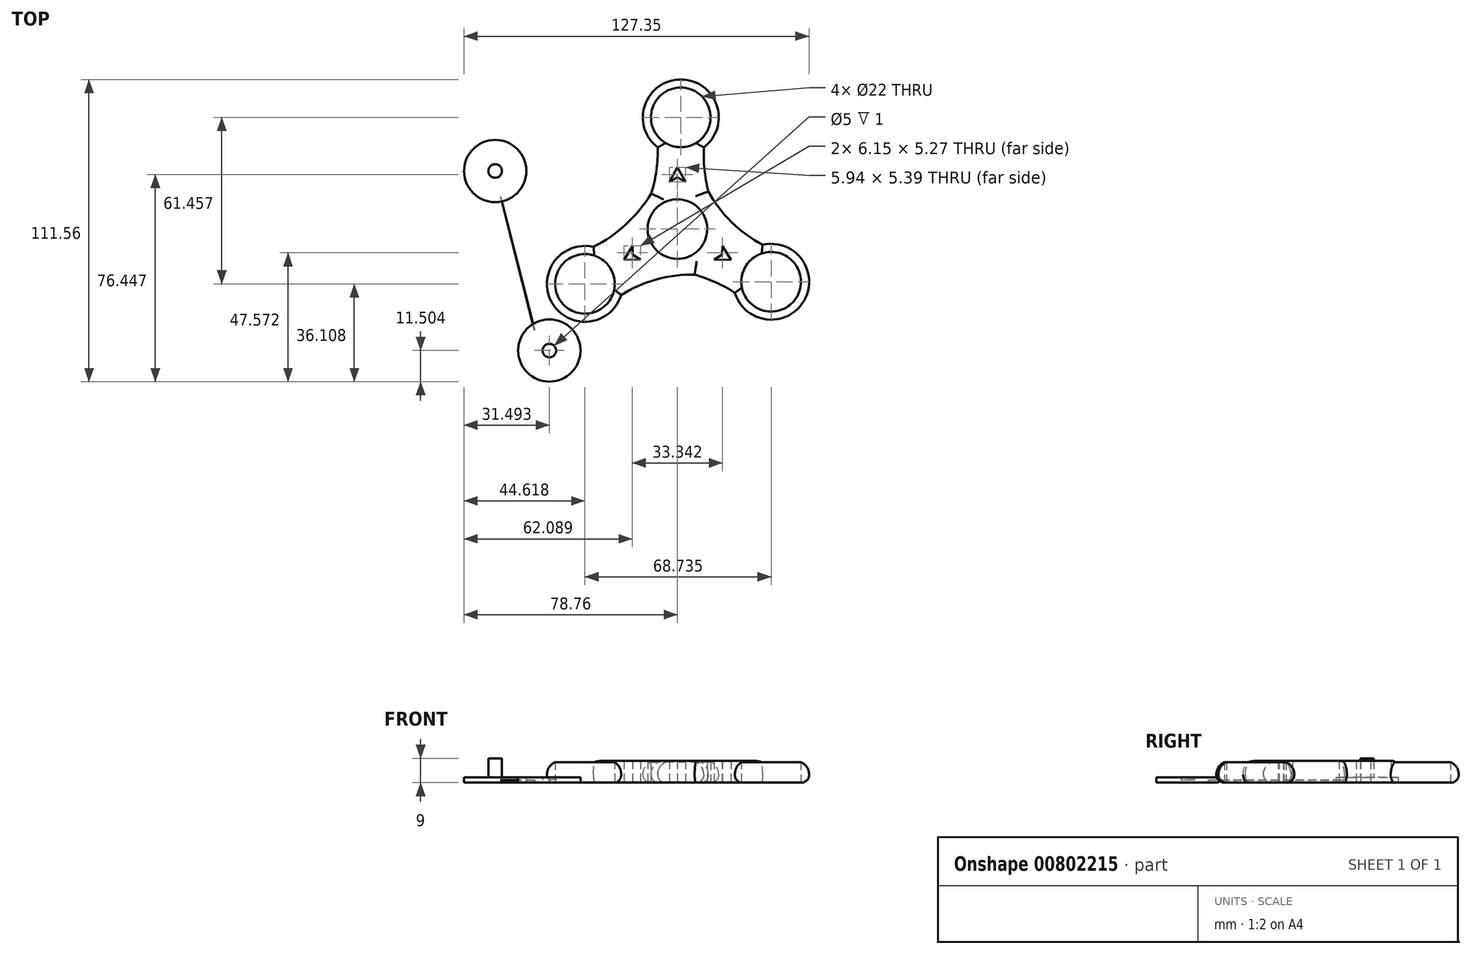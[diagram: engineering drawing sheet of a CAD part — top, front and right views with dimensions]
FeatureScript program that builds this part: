
annotation { "Feature Type Name" : "Feature", "Feature Type Description" : "" }
export const myFeature = defineFeature(function(context is Context, id is Id, definition is map)
    precondition{}
    {
        {
            var Q0;
            Q0=qCreatedBy(makeId("Top.planeOp"),FACE);
            var sketch = newSketch(context, id + "F0", { "sketchPlane" : qUnion([Q0])});
            skCircle(sketch, "E0", {"center": v(0, 0) * mm, "radius": 0.92 * mm});
            skCircle(sketch, "E1", {"center": v(0, 0) * mm, "radius": 11 * mm});
            skArc(sketch, "E2", {"start": v(-16.3, 0) * mm, "mid": v(-9.31, 14.32) * mm, "end": v(-7.3, 30.13) * mm});
            skArc(sketch, "E3", {"start": v(9.79, 30.13) * mm, "mid": v(1.24, 55.22) * mm, "end": v(-7.3, 30.13) * mm});
            skArc(sketch, "E4", {"start": v(9.79, 30.13) * mm, "mid": v(11.27, 14.51) * mm, "end": v(17.24, 0) * mm});
            skArc(sketch, "E5.1.0", {"start": v(-30.99, -6.6) * mm, "mid": v(-46.27, -27.23) * mm, "end": v(-20.75, -24.32) * mm});
            skArc(sketch, "E5.1.1", {"start": v(-30.99, -6.6) * mm, "mid": v(-18.2, 2.5) * mm, "end": v(-8.62, 14.93) * mm});
            skArc(sketch, "E5.1.2", {"start": v(9.85, -17.06) * mm, "mid": v(-6.05, -18.16) * mm, "end": v(-20.75, -24.32) * mm});
            skArc(sketch, "E5.2.0", {"start": v(21.2, -23.54) * mm, "mid": v(46.72, -26.45) * mm, "end": v(31.44, -5.81) * mm});
            skArc(sketch, "E5.2.1", {"start": v(21.2, -23.54) * mm, "mid": v(6.93, -17.01) * mm, "end": v(-8.62, -14.93) * mm});
            skArc(sketch, "E5.2.2", {"start": v(9.85, 17.06) * mm, "mid": v(18.75, 3.84) * mm, "end": v(31.44, -5.81) * mm});
            skCircle(sketch, "E6", {"center": v(1.24, 41.22) * mm, "radius": 11 * mm});
            skCircle(sketch, "E7", {"center": v(-34.14, -20.23) * mm, "radius": 11 * mm});
            skCircle(sketch, "E8", {"center": v(34.6, -19.45) * mm, "radius": 11 * mm});
            skLineSegment(sketch, "E9", {"start": v(0, 22.8) * mm, "end": v(-2.97, 17.41) * mm});
            skLineSegment(sketch, "E10", {"start": v(0, 22.8) * mm, "end": v(2.97, 17.41) * mm});
            skLineSegment(sketch, "E11", {"start": v(2.97, 17.41) * mm, "end": v(0, 19.05) * mm});
            skLineSegment(sketch, "E12", {"start": v(0, 19.05) * mm, "end": v(-2.97, 17.41) * mm});
            skLineSegment(sketch, "E13.1.0", {"start": v(-19.75, -11.4) * mm, "end": v(-16.56, -6.13) * mm});
            skLineSegment(sketch, "E13.1.1", {"start": v(-19.75, -11.4) * mm, "end": v(-13.6, -11.28) * mm});
            skLineSegment(sketch, "E13.1.2", {"start": v(-16.5, -9.52) * mm, "end": v(-13.6, -11.28) * mm});
            skLineSegment(sketch, "E13.1.3", {"start": v(-16.56, -6.13) * mm, "end": v(-16.5, -9.52) * mm});
            skLineSegment(sketch, "E13.2.0", {"start": v(19.75, -11.4) * mm, "end": v(13.6, -11.28) * mm});
            skLineSegment(sketch, "E13.2.1", {"start": v(19.75, -11.4) * mm, "end": v(16.56, -6.13) * mm});
            skLineSegment(sketch, "E13.2.2", {"start": v(16.5, -9.52) * mm, "end": v(16.56, -6.13) * mm});
            skLineSegment(sketch, "E13.2.3", {"start": v(13.6, -11.28) * mm, "end": v(16.5, -9.52) * mm});
            skSolve(sketch);
        }
        {
            var Q0;
            Q0 = qSketchRegion(id + "F0", true);
            extrude(context, id + "F1", {"entities" : qUnion([Q0]), "depth" : 8 * mm, "offsetDistance" : 25 * mm});
        }
        {
            var Q0;
            Q0=makeQuery(id+"F1.opExtrude","CAP_EDGE",EDGE,{"disambiguationData":[OSD([sQuery(id+"F0.wireOp",EDGE,"E3")])],"isStart":false});
            var Q1;
            Q1=makeQuery(id+"F1.opExtrude","CAP_EDGE",EDGE,{"disambiguationData":[OSD([sQuery(id+"F0.wireOp",EDGE,"E4")])],"isStart":false});
            var Q2;
            Q2=makeQuery(id+"F1.opExtrude","CAP_EDGE",EDGE,{"disambiguationData":[OSD([sQuery(id+"F0.wireOp",EDGE,"E5.2.2")])],"isStart":false});
            var Q3;
            Q3=makeQuery(id+"F1.opExtrude","CAP_EDGE",EDGE,{"disambiguationData":[OSD([sQuery(id+"F0.wireOp",EDGE,"E5.2.0")])],"isStart":false});
            var Q4;
            Q4=makeQuery(id+"F1.opExtrude","CAP_EDGE",EDGE,{"disambiguationData":[OSD([sQuery(id+"F0.wireOp",EDGE,"E5.2.1")])],"isStart":false});
            var Q5;
            Q5=makeQuery(id+"F1.opExtrude","CAP_EDGE",EDGE,{"disambiguationData":[OSD([sQuery(id+"F0.wireOp",EDGE,"E5.1.2")])],"isStart":false});
            var Q6;
            Q6=makeQuery(id+"F1.opExtrude","CAP_EDGE",EDGE,{"disambiguationData":[OSD([sQuery(id+"F0.wireOp",EDGE,"E5.1.0")])],"isStart":false});
            var Q7;
            Q7=makeQuery(id+"F1.opExtrude","CAP_EDGE",EDGE,{"disambiguationData":[OSD([sQuery(id+"F0.wireOp",EDGE,"E5.1.1")])],"isStart":false});
            var Q8;
            Q8=makeQuery(id+"F1.opExtrude","CAP_EDGE",EDGE,{"disambiguationData":[OSD([sQuery(id+"F0.wireOp",EDGE,"E2")])],"isStart":false});
            fillet(context, id + "F2", {"entities" : qUnion([Q0, Q1, Q2, Q3, Q4, Q5, Q6, Q7, Q8]), "radius" : 5 * mm, "tangentPropagation" : true, "allowEdgeOverflow" : false});
        }
        {
            var Q0;
            Q0=makeQuery(id+"F1.opExtrude","CAP_EDGE",EDGE,{"disambiguationData":[OSD([sQuery(id+"F0.wireOp",EDGE,"E2")])],"isStart":true});
            var Q1;
            Q1=makeQuery(id+"F1.opExtrude","CAP_EDGE",EDGE,{"disambiguationData":[OSD([sQuery(id+"F0.wireOp",EDGE,"E5.1.1")])],"isStart":true});
            var Q2;
            Q2=makeQuery(id+"F1.opExtrude","CAP_EDGE",EDGE,{"disambiguationData":[OSD([sQuery(id+"F0.wireOp",EDGE,"E5.1.2")])],"isStart":true});
            var Q3;
            Q3=makeQuery(id+"F1.opExtrude","CAP_EDGE",EDGE,{"disambiguationData":[OSD([sQuery(id+"F0.wireOp",EDGE,"E5.2.1")])],"isStart":true});
            var Q4;
            Q4=makeQuery(id+"F1.opExtrude","CAP_EDGE",EDGE,{"disambiguationData":[OSD([sQuery(id+"F0.wireOp",EDGE,"E4")])],"isStart":true});
            var Q5;
            Q5=makeQuery(id+"F1.opExtrude","CAP_EDGE",EDGE,{"disambiguationData":[OSD([sQuery(id+"F0.wireOp",EDGE,"E5.1.0")])],"isStart":true});
            var Q6;
            Q6=makeQuery(id+"F1.opExtrude","CAP_EDGE",EDGE,{"disambiguationData":[OSD([sQuery(id+"F0.wireOp",EDGE,"E5.2.0")])],"isStart":true});
            var Q7;
            Q7=makeQuery(id+"F1.opExtrude","CAP_EDGE",EDGE,{"disambiguationData":[OSD([sQuery(id+"F0.wireOp",EDGE,"E3")])],"isStart":true});
            var Q8;
            Q8=makeQuery(id+"F1.opExtrude","CAP_EDGE",EDGE,{"disambiguationData":[OSD([sQuery(id+"F0.wireOp",EDGE,"E5.2.2")])],"isStart":true});
            fillet(context, id + "F3", {"entities" : qUnion([Q0, Q1, Q2, Q3, Q4, Q5, Q6, Q7, Q8]), "radius" : 2.9 * mm, "tangentPropagation" : true, "allowEdgeOverflow" : false});
        }
        {
            var Q0;
            Q0=qCreatedBy(makeId("Top.planeOp"),FACE);
            var sketch = newSketch(context, id + "F4", { "sketchPlane" : qUnion([Q0])});
            skCircle(sketch, "E14", {"center": v(-67.26, 21.43) * mm, "radius": 11.5 * mm});
            skCircle(sketch, "E15", {"center": v(-67.26, 21.43) * mm, "radius": 2.5 * mm});
            skSolve(sketch);
        }
        {
            var Q0;
            Q0=makeQuery(id+"F4.imprint","IMPRINT",FACE,{"disambiguationData":[TD([[makeQuery(id+"F4.imprint","IMPRINT",EDGE,{"derivedFrom":sQuery(id+"F4.wireOp",EDGE,"E14")}),1.0]])]});
            extrude(context, id + "F5", {"entities" : qUnion([Q0]), "depth" : 2 * mm, "offsetDistance" : 25 * mm});
        }
        {
            var Q0;
            Q0=makeQuery(id+"F4.imprint","IMPRINT",FACE,{"disambiguationData":[TD([[makeQuery(id+"F4.imprint","IMPRINT",EDGE,{"derivedFrom":sQuery(id+"F4.wireOp",EDGE,"E15")}),1.0]])]});
            extrude(context, id + "F6", {"entities" : qUnion([Q0]), "operationType" : NewBodyOperationType.ADD, "depth" : 9 * mm, "offsetDistance" : 25 * mm});
        }
        {
            var Q0;
            Q0=qCreatedBy(makeId("Top.planeOp"),FACE);
            var sketch = newSketch(context, id + "F7", { "sketchPlane" : qUnion([Q0])});
            skCircle(sketch, "E16", {"center": v(-47.27, -44.84) * mm, "radius": 11.5 * mm});
            skCircle(sketch, "E17", {"center": v(-47.27, -44.84) * mm, "radius": 2.5 * mm});
            skSolve(sketch);
        }
        {
            var Q0;
            Q0 = qSketchRegion(id + "F7", true);
            extrude(context, id + "F8", {"entities" : qUnion([Q0]), "depth" : 2 * mm, "offsetDistance" : 25 * mm});
        }
        {
            var Q0;
            Q0=makeQuery(id+"F7.imprint","IMPRINT",FACE,{"disambiguationData":[TD([[makeQuery(id+"F7.imprint","IMPRINT",EDGE,{"derivedFrom":sQuery(id+"F7.wireOp",EDGE,"E17")}),1.0]])]});
            extrude(context, id + "F9", {"entities" : qUnion([Q0]), "operationType" : NewBodyOperationType.ADD, "depth" : 1 * mm, "offsetDistance" : 25 * mm});
        }
        {
            var Q0;
            Q0=qCreatedBy(makeId("Top.planeOp"),FACE);
            var sketch = newSketch(context, id + "F10", { "sketchPlane" : qUnion([Q0])});
            skLineSegment(sketch, "E18", {"start": v(-65.26, 12.04) * mm, "end": v(-52.63, -37.25) * mm});
            skLineSegment(sketch, "E19", {"start": v(-52.63, -37.25) * mm, "end": v(-52.85, -37.3) * mm});
            skLineSegment(sketch, "E20", {"start": v(-52.85, -37.3) * mm, "end": v(-65.26, 12.04) * mm});
            skSolve(sketch);
        }
        {
            var Q0;
            Q0=makeQuery(id+"F10.imprint","IMPRINT",FACE,{"disambiguationData":[TD([[makeQuery(id+"F10.imprint","IMPRINT",EDGE,{"derivedFrom":sQuery(id+"F10.wireOp",EDGE,"E18")}),-1.0]])]});
            extrude(context, id + "F11", {"entities" : qUnion([Q0]), "depth" : 0.9 * mm, "offsetDistance" : 25 * mm});
        }
    });
